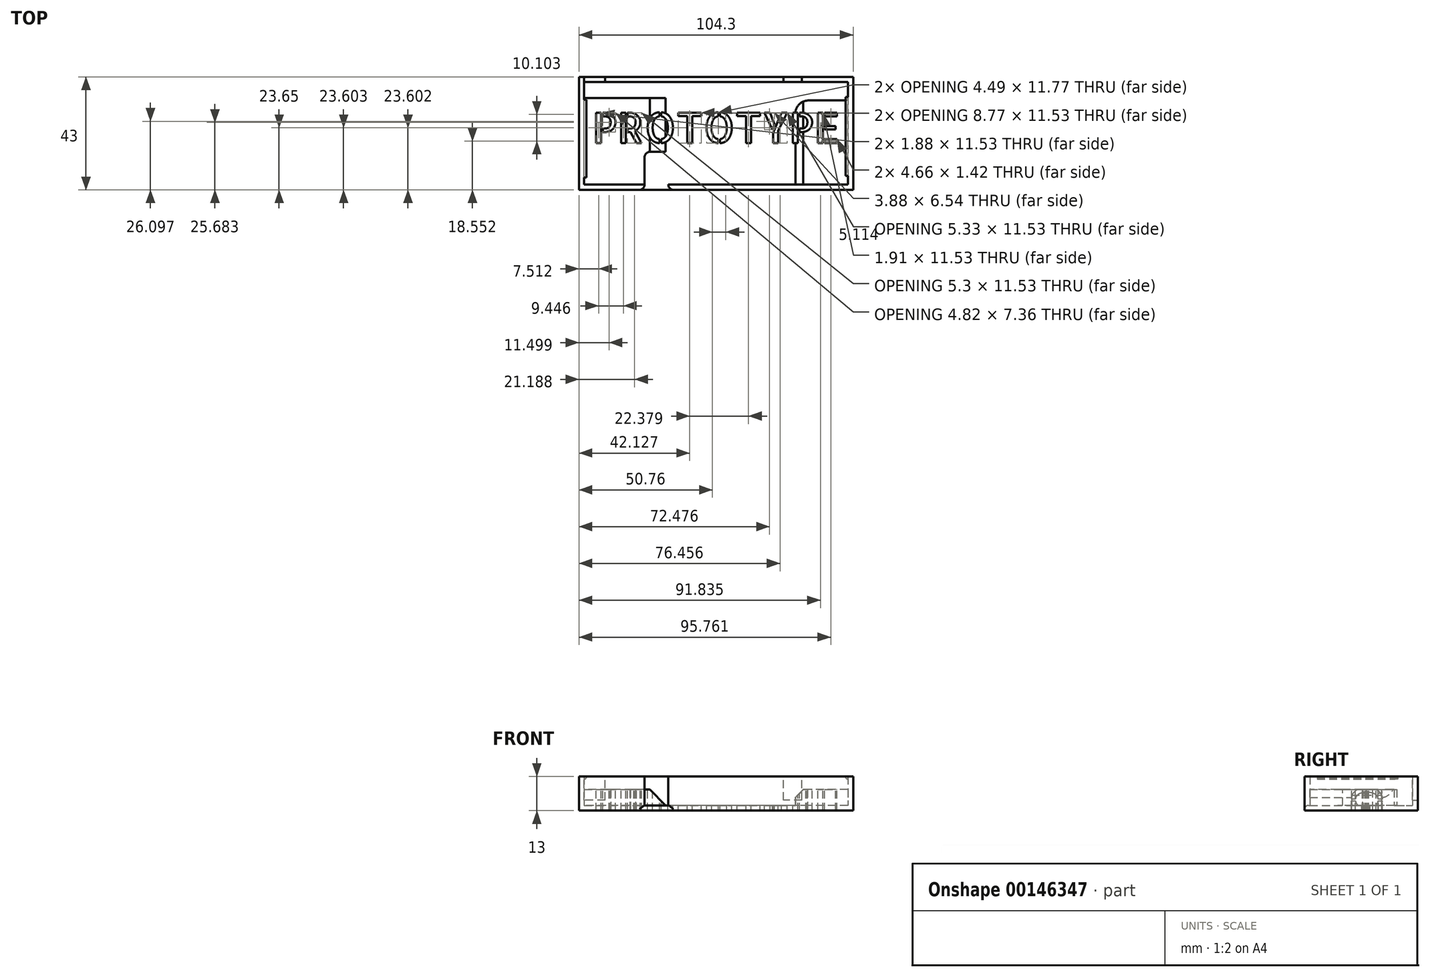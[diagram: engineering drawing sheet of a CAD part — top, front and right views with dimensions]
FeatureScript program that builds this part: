
annotation { "Feature Type Name" : "Feature", "Feature Type Description" : "" }
export const myFeature = defineFeature(function(context is Context, id is Id, definition is map)
    precondition{}
    {
        {
            var Q0;
            Q0=qCreatedBy(makeId("Top.planeOp"),FACE);
            var sketch = newSketch(context, id + "F0", { "sketchPlane" : qUnion([Q0])});
            skLineSegment(sketch, "E0.bottom", {"start": v(52.15, -21.5) * mm, "end": v(-52.15, -21.5) * mm});
            skLineSegment(sketch, "E0.top", {"start": v(52.15, 21.5) * mm, "end": v(-52.15, 21.5) * mm});
            skLineSegment(sketch, "E0.left", {"start": v(52.15, -21.5) * mm, "end": v(52.15, 21.5) * mm});
            skLineSegment(sketch, "E0.right", {"start": v(-52.15, -21.5) * mm, "end": v(-52.15, 21.5) * mm});
            skPoint(sketch, "E0.middle", {"position": v(0, 0) * mm});
            skSolve(sketch);
        }
        {
            var Q0;
            Q0=makeQuery(id+"F0.imprint","IMPRINT",FACE,{"disambiguationData":[TD([[makeQuery(id+"F0.imprint","IMPRINT",EDGE,{"derivedFrom":sQuery(id+"F0.wireOp",EDGE,"E0.bottom")}),-1.0]])]});
            extrude(context, id + "F1", {"entities" : qUnion([Q0]), "depth" : 13 * mm});
        }
        {
            var Q0;
            Q0=makeQuery(id+"F1.opExtrude","CAP_FACE",FACE,{"disambiguationData":[OSD([sQuery(id+"F0.wireOp",EDGE,"E0.bottom"),sQuery(id+"F0.wireOp",EDGE,"E0.top"),sQuery(id+"F0.wireOp",EDGE,"E0.left"),sQuery(id+"F0.wireOp",EDGE,"E0.right")])],"isStart":false});
            shell(context, id + "F2", {"entities" : qUnion([Q0]), "thickness" : 2 * mm});
        }
        {
            var Q0;
            Q0=makeQuery(id+"F1.opExtrude","CAP_FACE",FACE,{"disambiguationData":[OSD([sQuery(id+"F0.wireOp",EDGE,"E0.bottom"),sQuery(id+"F0.wireOp",EDGE,"E0.top"),sQuery(id+"F0.wireOp",EDGE,"E0.left"),sQuery(id+"F0.wireOp",EDGE,"E0.right")])],"isStart":false});
            var sketch = newSketch(context, id + "F3", { "sketchPlane" : qUnion([Q0])});
            skLineSegment(sketch, "E1.bottom", {"start": v(-50.15, 19.5) * mm, "end": v(-42.15, 19.5) * mm});
            skLineSegment(sketch, "E1.top", {"start": v(-50.15, 23.74) * mm, "end": v(-42.15, 23.74) * mm});
            skLineSegment(sketch, "E1.left", {"start": v(-50.15, 19.5) * mm, "end": v(-50.15, 23.74) * mm});
            skLineSegment(sketch, "E1.right", {"start": v(-42.15, 19.5) * mm, "end": v(-42.15, 23.74) * mm});
            skPoint(sketch, "E2", {"position": v(32.65, 19.5) * mm});
            skLineSegment(sketch, "E3.bottom", {"start": v(32.65, 19.5) * mm, "end": v(25.65, 19.5) * mm});
            skLineSegment(sketch, "E3.top", {"start": v(32.65, 24.19) * mm, "end": v(25.65, 24.19) * mm});
            skLineSegment(sketch, "E3.left", {"start": v(32.65, 19.5) * mm, "end": v(32.65, 24.19) * mm});
            skLineSegment(sketch, "E3.right", {"start": v(25.65, 19.5) * mm, "end": v(25.65, 24.19) * mm});
            skSolve(sketch);
        }
        {
            var Q0;
            Q0 = qSketchRegion(id + "F3", true);
            extrude(context, id + "F4", {"entities" : qUnion([Q0]), "operationType" : NewBodyOperationType.REMOVE, "oppositeDirection" : true, "depth" : 9 * mm});
        }
        {
            var Q0;
            Q0=makeQuery(id+"F2.opShell","OFFSET_FACE",FACE,{"disambiguationData":[OSD([sQuery(id+"F0.wireOp",EDGE,"E0.bottom"),sQuery(id+"F0.wireOp",EDGE,"E0.top"),sQuery(id+"F0.wireOp",EDGE,"E0.left"),sQuery(id+"F0.wireOp",EDGE,"E0.right")])]});
            var sketch = newSketch(context, id + "F5", { "sketchPlane" : qUnion([Q0])});
            skLineSegment(sketch, "E4.bottom", {"start": v(-50.15, -19.5) * mm, "end": v(-18.15, -19.5) * mm});
            skLineSegment(sketch, "E4.top", {"start": v(-50.15, 13.5) * mm, "end": v(-18.15, 13.5) * mm});
            skLineSegment(sketch, "E4.left", {"start": v(-50.15, -19.5) * mm, "end": v(-50.15, 13.5) * mm});
            skLineSegment(sketch, "E4.right", {"start": v(-18.15, -19.5) * mm, "end": v(-18.15, 13.5) * mm});
            skSolve(sketch);
        }
        {
            var Q0;
            Q0 = qSketchRegion(id + "F5", true);
            extrude(context, id + "F6", {"entities" : qUnion([Q0]), "operationType" : NewBodyOperationType.ADD, "depth" : 6 * mm});
        }
        {
            var Q0;
            Q0=makeQuery(id+"F6.opExtrude","CAP_FACE",FACE,{"disambiguationData":[OSD([sQuery(id+"F5.wireOp",EDGE,"E4.bottom"),sQuery(id+"F5.wireOp",EDGE,"E4.top"),sQuery(id+"F5.wireOp",EDGE,"E4.left"),sQuery(id+"F5.wireOp",EDGE,"E4.right")])],"isStart":false});
            var sketch = newSketch(context, id + "F7", { "sketchPlane" : qUnion([Q0])});
            skLineSegment(sketch, "E5.bottom", {"start": v(-18.15, -19.5) * mm, "end": v(-27.15, -19.5) * mm});
            skLineSegment(sketch, "E5.top", {"start": v(-18.15, -7) * mm, "end": v(-27.15, -7) * mm});
            skLineSegment(sketch, "E5.left", {"start": v(-18.15, -19.5) * mm, "end": v(-18.15, -7) * mm});
            skLineSegment(sketch, "E5.right", {"start": v(-27.15, -19.5) * mm, "end": v(-27.15, -7) * mm});
            skSolve(sketch);
        }
        {
            var Q0;
            Q0 = qSketchRegion(id + "F7", true);
            extrude(context, id + "F8", {"entities" : qUnion([Q0]), "operationType" : NewBodyOperationType.REMOVE, "oppositeDirection" : true, "depth" : 6 * mm});
        }
        {
            var Q0;
            Q0=makeQuery(id+"F6.opExtrude","CAP_FACE",FACE,{"disambiguationData":[OSD([sQuery(id+"F5.wireOp",EDGE,"E4.bottom"),sQuery(id+"F5.wireOp",EDGE,"E4.top"),sQuery(id+"F5.wireOp",EDGE,"E4.left"),sQuery(id+"F5.wireOp",EDGE,"E4.right")])],"isStart":false});
            var sketch = newSketch(context, id + "F9", { "sketchPlane" : qUnion([Q0])});
            skLineSegment(sketch, "E6.bottom", {"start": v(-27.15, -7) * mm, "end": v(-18.15, -7) * mm});
            skLineSegment(sketch, "E6.top", {"start": v(-27.15, -27.58) * mm, "end": v(-18.15, -27.58) * mm});
            skLineSegment(sketch, "E6.left", {"start": v(-27.15, -7) * mm, "end": v(-27.15, -27.58) * mm});
            skLineSegment(sketch, "E6.right", {"start": v(-18.15, -7) * mm, "end": v(-18.15, -27.58) * mm});
            skSolve(sketch);
        }
        {
            var Q0;
            Q0 = qSketchRegion(id + "F9", true);
            extrude(context, id + "F10", {"entities" : qUnion([Q0]), "operationType" : NewBodyOperationType.REMOVE, "oppositeDirection" : true, "depth" : 6 * mm, "hasSecondDirection" : true, "secondDirectionOppositeDirection" : false, "secondDirectionDepth" : 25.4 * mm});
        }
        {
            var Q0;
            Q0=makeQuery(id+"F6.opExtrude","CAP_EDGE",EDGE,{"disambiguationData":[OSD([sQuery(id+"F5.wireOp",EDGE,"E4.right")])],"isStart":false});
            chamfer(context, id + "F11", {"entities" : qUnion([Q0]), "width" : 7 * mm, "tangentPropagation" : true});
        }
        {
            var Q0;
            Q0=makeQuery(id+"F8.boolean.opBoolean","COPY",EDGE,{"derivedFrom":makeQuery(id+"F8.opExtrude","SWEPT_EDGE",EDGE,{"disambiguationData":[OSD([sQuery(id+"F7.wireOp",EDGE,"E5.top"),sQuery(id+"F7.wireOp",EDGE,"E5.right")])]})});
            fillet(context, id + "F12", {"entities" : qUnion([Q0]), "radius" : 2 * mm, "tangentPropagation" : true, "allowEdgeOverflow" : false});
        }
        {
            var Q0;
            Q0=makeQuery(id+"F10.boolean.opBoolean","INTERSECT",EDGE,{"derivedFrom":[makeQuery(id+"F1.opExtrude","SWEPT_FACE",FACE,{"disambiguationData":[OSD([sQuery(id+"F0.wireOp",EDGE,"E0.bottom")])]}),makeQuery(id+"F10.opExtrude","CAP_FACE",FACE,{"disambiguationData":[OSD([sQuery(id+"F9.wireOp",EDGE,"E6.bottom"),sQuery(id+"F9.wireOp",EDGE,"E6.top"),sQuery(id+"F9.wireOp",EDGE,"E6.left"),sQuery(id+"F9.wireOp",EDGE,"E6.right")])],"isStart":false})]});
            fillet(context, id + "F13", {"entities" : qUnion([Q0]), "radius" : 1.5 * mm, "tangentPropagation" : true, "allowEdgeOverflow" : false});
        }
        {
            var Q0;
            Q0=makeQuery(id+"F10.boolean.opBoolean","MERGE",FACE,{"derivedFrom":[makeQuery(id+"F8.boolean.opBoolean","MERGE",FACE,{"derivedFrom":[makeQuery(id+"F2.opShell","OFFSET_FACE",FACE,{"disambiguationData":[OSD([sQuery(id+"F0.wireOp",EDGE,"E0.bottom"),sQuery(id+"F0.wireOp",EDGE,"E0.top"),sQuery(id+"F0.wireOp",EDGE,"E0.left"),sQuery(id+"F0.wireOp",EDGE,"E0.right")])]}),makeQuery(id+"F8.opExtrude","CAP_FACE",FACE,{"disambiguationData":[OSD([sQuery(id+"F7.wireOp",EDGE,"E5.bottom"),sQuery(id+"F7.wireOp",EDGE,"E5.top"),sQuery(id+"F7.wireOp",EDGE,"E5.left"),sQuery(id+"F7.wireOp",EDGE,"E5.right")])],"isStart":false})]}),makeQuery(id+"F10.opExtrude","CAP_FACE",FACE,{"disambiguationData":[OSD([sQuery(id+"F9.wireOp",EDGE,"E6.bottom"),sQuery(id+"F9.wireOp",EDGE,"E6.top"),sQuery(id+"F9.wireOp",EDGE,"E6.left"),sQuery(id+"F9.wireOp",EDGE,"E6.right")])],"isStart":false})]});
            var sketch = newSketch(context, id + "F14", { "sketchPlane" : qUnion([Q0])});
            skLineSegment(sketch, "E7.bottom", {"start": v(50.15, -19.5) * mm, "end": v(30.15, -19.5) * mm});
            skLineSegment(sketch, "E7.top", {"start": v(50.15, 12.5) * mm, "end": v(30.15, 12.5) * mm});
            skLineSegment(sketch, "E7.left", {"start": v(50.15, -19.5) * mm, "end": v(50.15, 12.5) * mm});
            skLineSegment(sketch, "E7.right", {"start": v(30.15, -19.5) * mm, "end": v(30.15, 12.5) * mm});
            skSolve(sketch);
        }
        {
            var Q0;
            Q0 = qSketchRegion(id + "F14", true);
            extrude(context, id + "F15", {"entities" : qUnion([Q0]), "operationType" : NewBodyOperationType.ADD, "depth" : 6 * mm});
        }
        {
            var Q0;
            Q0=makeQuery(id+"F15.opExtrude","SWEPT_EDGE",EDGE,{"disambiguationData":[OSD([sQuery(id+"F14.wireOp",EDGE,"E7.top"),sQuery(id+"F14.wireOp",EDGE,"E7.right")])]});
            fillet(context, id + "F16", {"entities" : qUnion([Q0]), "radius" : 5 * mm, "tangentPropagation" : true, "allowEdgeOverflow" : false});
        }
        {
            var Q0;
            Q0=makeQuery(id+"F15.opExtrude","CAP_EDGE",EDGE,{"disambiguationData":[OSD([sQuery(id+"F14.wireOp",EDGE,"E7.right")])],"isStart":false});
            chamfer(context, id + "F17", {"entities" : qUnion([Q0]), "width" : 3 * mm});
        }
        {
            var Q0;
            Q0=makeQuery(id+"F10.boolean.opBoolean","INTERSECT",EDGE,{"derivedFrom":[makeQuery(id+"F1.opExtrude","SWEPT_FACE",FACE,{"disambiguationData":[OSD([sQuery(id+"F0.wireOp",EDGE,"E0.bottom")])]}),makeQuery(id+"F10.opExtrude","SWEPT_FACE",FACE,{"disambiguationData":[OSD([sQuery(id+"F9.wireOp",EDGE,"E6.left")])]})]});
            var Q1;
            Q1=makeQuery(id+"F10.boolean.opBoolean","INTERSECT",EDGE,{"derivedFrom":[makeQuery(id+"F1.opExtrude","SWEPT_FACE",FACE,{"disambiguationData":[OSD([sQuery(id+"F0.wireOp",EDGE,"E0.bottom")])]}),makeQuery(id+"F10.opExtrude","SWEPT_FACE",FACE,{"disambiguationData":[OSD([sQuery(id+"F9.wireOp",EDGE,"E6.right")])]})]});
            fillet(context, id + "F18", {"entities" : qUnion([Q0, Q1]), "radius" : 2 * mm, "tangentPropagation" : true, "allowEdgeOverflow" : false});
        }
        {
            var Q0;
            Q0=makeQuery(id+"F1.opExtrude","SWEPT_FACE",FACE,{"disambiguationData":[OSD([sQuery(id+"F0.wireOp",EDGE,"E0.right")])]});
            var sketch = newSketch(context, id + "F19", { "sketchPlane" : qUnion([Q0])});
            skLineSegment(sketch, "E8.bottom", {"start": v(16.75, 13) * mm, "end": v(-12.85, 13) * mm});
            skLineSegment(sketch, "E8.top", {"start": v(16.75, 12) * mm, "end": v(-12.85, 12) * mm});
            skLineSegment(sketch, "E8.left", {"start": v(16.75, 13) * mm, "end": v(16.75, 12) * mm});
            skLineSegment(sketch, "E8.right", {"start": v(-12.85, 13) * mm, "end": v(-12.85, 12) * mm});
            skSolve(sketch);
        }
        {
            var Q0;
            Q0 = qSketchRegion(id + "F19", true);
            extrude(context, id + "F20", {"entities" : qUnion([Q0]), "operationType" : NewBodyOperationType.ADD, "oppositeDirection" : true, "depth" : 3 * mm});
        }
        {
            var Q0;
            Q0=makeQuery(id+"F20.opExtrude","CAP_EDGE",EDGE,{"disambiguationData":[OSD([sQuery(id+"F19.wireOp",EDGE,"E8.top")])],"isStart":false});
            var Q1;
            Q1=makeQuery(id+"F20.opExtrude","CAP_EDGE",EDGE,{"disambiguationData":[OSD([sQuery(id+"F19.wireOp",EDGE,"E8.bottom")])],"isStart":false});
            fillet(context, id + "F21", {"entities" : qUnion([Q0, Q1]), "radius" : 1 * mm, "tangentPropagation" : true, "allowEdgeOverflow" : false});
        }
        {
            var Q0;
            Q0=makeQuery(id+"F1.opExtrude","SWEPT_FACE",FACE,{"disambiguationData":[OSD([sQuery(id+"F0.wireOp",EDGE,"E0.left")])]});
            var sketch = newSketch(context, id + "F22", { "sketchPlane" : qUnion([Q0])});
            skLineSegment(sketch, "E9.bottom", {"start": v(-16.19, 13) * mm, "end": v(13.86, 13) * mm});
            skLineSegment(sketch, "E9.top", {"start": v(-16.19, 12) * mm, "end": v(13.86, 12) * mm});
            skLineSegment(sketch, "E9.left", {"start": v(-16.19, 13) * mm, "end": v(-16.19, 12) * mm});
            skLineSegment(sketch, "E9.right", {"start": v(13.86, 13) * mm, "end": v(13.86, 12) * mm});
            skSolve(sketch);
        }
        {
            var Q0;
            Q0 = qSketchRegion(id + "F22", true);
            extrude(context, id + "F23", {"entities" : qUnion([Q0]), "operationType" : NewBodyOperationType.ADD, "oppositeDirection" : true, "depth" : 3 * mm});
        }
        {
            var Q0;
            Q0=makeQuery(id+"F23.opExtrude","CAP_EDGE",EDGE,{"disambiguationData":[OSD([sQuery(id+"F22.wireOp",EDGE,"E9.top")])],"isStart":false});
            var Q1;
            Q1=makeQuery(id+"F23.opExtrude","CAP_EDGE",EDGE,{"disambiguationData":[OSD([sQuery(id+"F22.wireOp",EDGE,"E9.bottom")])],"isStart":false});
            fillet(context, id + "F24", {"entities" : qUnion([Q0, Q1]), "radius" : 1 * mm, "tangentPropagation" : true, "allowEdgeOverflow" : false});
        }
        {
            var Q0;
            Q0=makeQuery(id+"F10.boolean.opBoolean","MERGE",FACE,{"derivedFrom":[makeQuery(id+"F8.boolean.opBoolean","MERGE",FACE,{"derivedFrom":[makeQuery(id+"F2.opShell","OFFSET_FACE",FACE,{"disambiguationData":[OSD([sQuery(id+"F0.wireOp",EDGE,"E0.bottom"),sQuery(id+"F0.wireOp",EDGE,"E0.top"),sQuery(id+"F0.wireOp",EDGE,"E0.left"),sQuery(id+"F0.wireOp",EDGE,"E0.right")])]}),makeQuery(id+"F8.opExtrude","CAP_FACE",FACE,{"disambiguationData":[OSD([sQuery(id+"F7.wireOp",EDGE,"E5.bottom"),sQuery(id+"F7.wireOp",EDGE,"E5.top"),sQuery(id+"F7.wireOp",EDGE,"E5.left"),sQuery(id+"F7.wireOp",EDGE,"E5.right")])],"isStart":false})]}),makeQuery(id+"F10.opExtrude","CAP_FACE",FACE,{"disambiguationData":[OSD([sQuery(id+"F9.wireOp",EDGE,"E6.bottom"),sQuery(id+"F9.wireOp",EDGE,"E6.top"),sQuery(id+"F9.wireOp",EDGE,"E6.left"),sQuery(id+"F9.wireOp",EDGE,"E6.right")])],"isStart":false})]});
            var sketch = newSketch(context, id + "F25", { "sketchPlane" : qUnion([Q0])});
            skText(sketch, "E10", { "text": "PROTOTYPE", "fontName": "AllertaStencil-Regular.ttf"});
            const initialGuessF25  = {"E10": [-0.047, -0.00366, 1, 0, 0.01153]};
            skSetInitialGuess(sketch, initialGuessF25);
            skSolve(sketch);
        }
        {
            var Q0;
            Q0 = qSketchRegion(id + "F25", true);
            extrude(context, id + "F26", {"entities" : qUnion([Q0]), "operationType" : NewBodyOperationType.REMOVE, "endBound" : BoundingType.SYMMETRIC, "oppositeDirection" : true, "depth" : 25.4 * mm});
        }
    });
